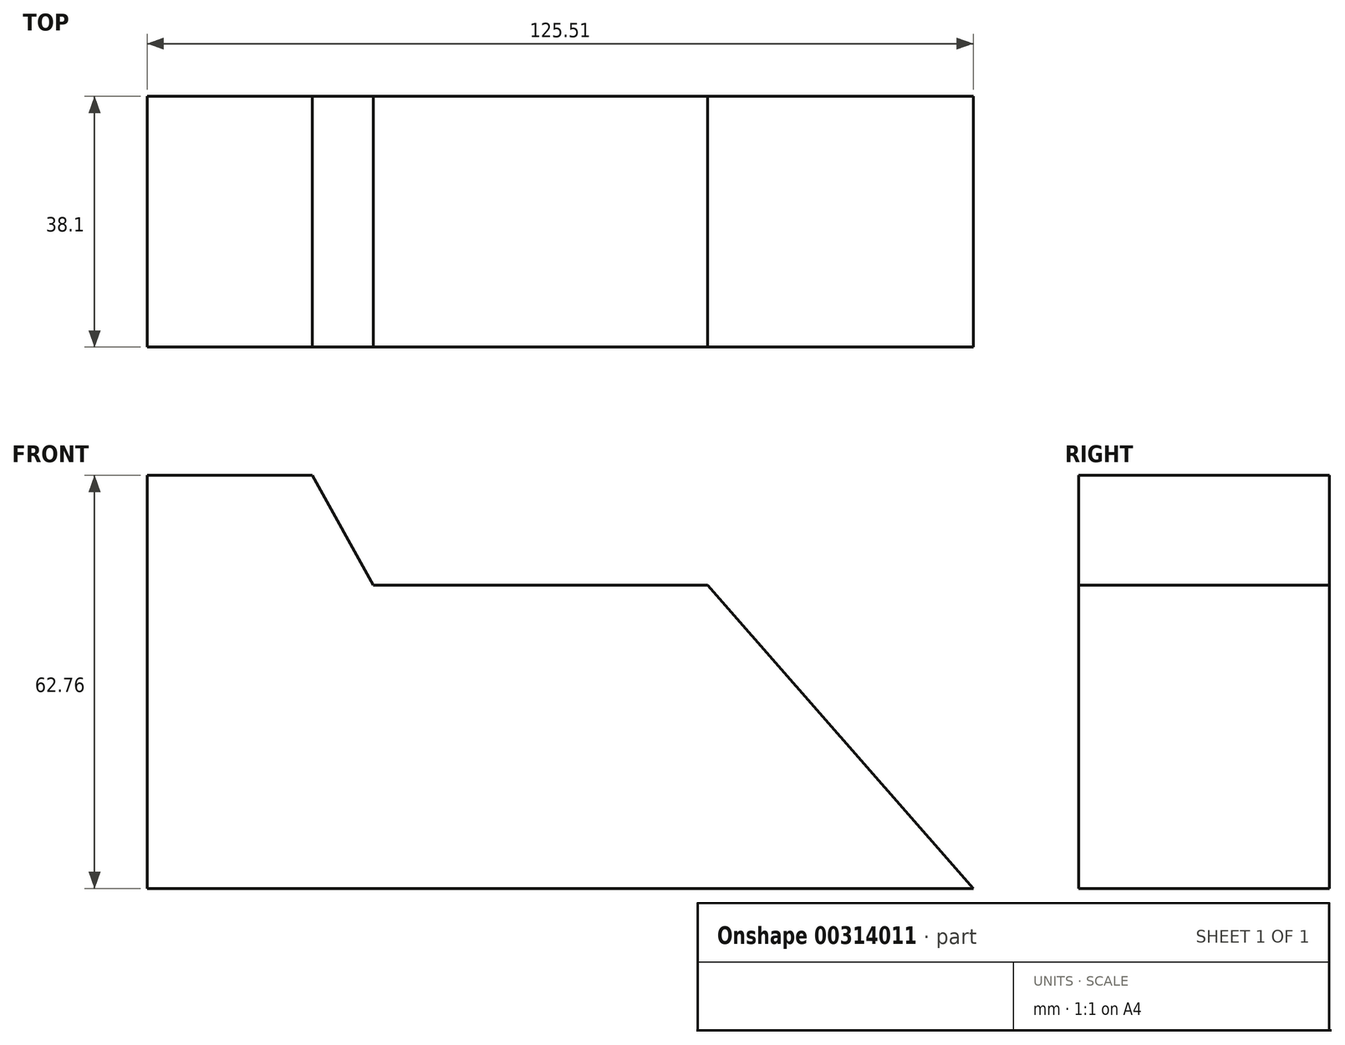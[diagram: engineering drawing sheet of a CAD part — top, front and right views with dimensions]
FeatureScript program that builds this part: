
annotation { "Feature Type Name" : "Feature", "Feature Type Description" : "" }
export const myFeature = defineFeature(function(context is Context, id is Id, definition is map)
    precondition{}
    {
        {
            var Q0;
            Q0=qCreatedBy(makeId("Front.planeOp"),FACE);
            var sketch = newSketch(context, id + "F0", { "sketchPlane" : qUnion([Q0])});
            skLineSegment(sketch, "E0", {"start": v(-66, 39.22) * mm, "end": v(-40.9, 39.22) * mm});
            skLineSegment(sketch, "E1", {"start": v(-66, -23.54) * mm, "end": v(59.51, -23.54) * mm});
            skLineSegment(sketch, "E2", {"start": v(-66, 39.22) * mm, "end": v(-66, -23.54) * mm});
            skLineSegment(sketch, "E3", {"start": v(-31.64, 22.57) * mm, "end": v(19.16, 22.57) * mm});
            skLineSegment(sketch, "E4", {"start": v(-40.9, 39.22) * mm, "end": v(-31.64, 22.57) * mm});
            skLineSegment(sketch, "E5", {"start": v(19.16, 22.57) * mm, "end": v(59.51, -23.54) * mm});
            skSolve(sketch);
        }
        {
            var Q0;
            Q0=makeQuery(id+"F0.imprint","IMPRINT",FACE,{"disambiguationData":[TD([[makeQuery(id+"F0.imprint","IMPRINT",EDGE,{"derivedFrom":sQuery(id+"F0.wireOp",EDGE,"E0")}),-1.0]])]});
            extrude(context, id + "F1", {"entities" : qUnion([Q0]), "depth" : 38.1 * mm});
        }
    });
